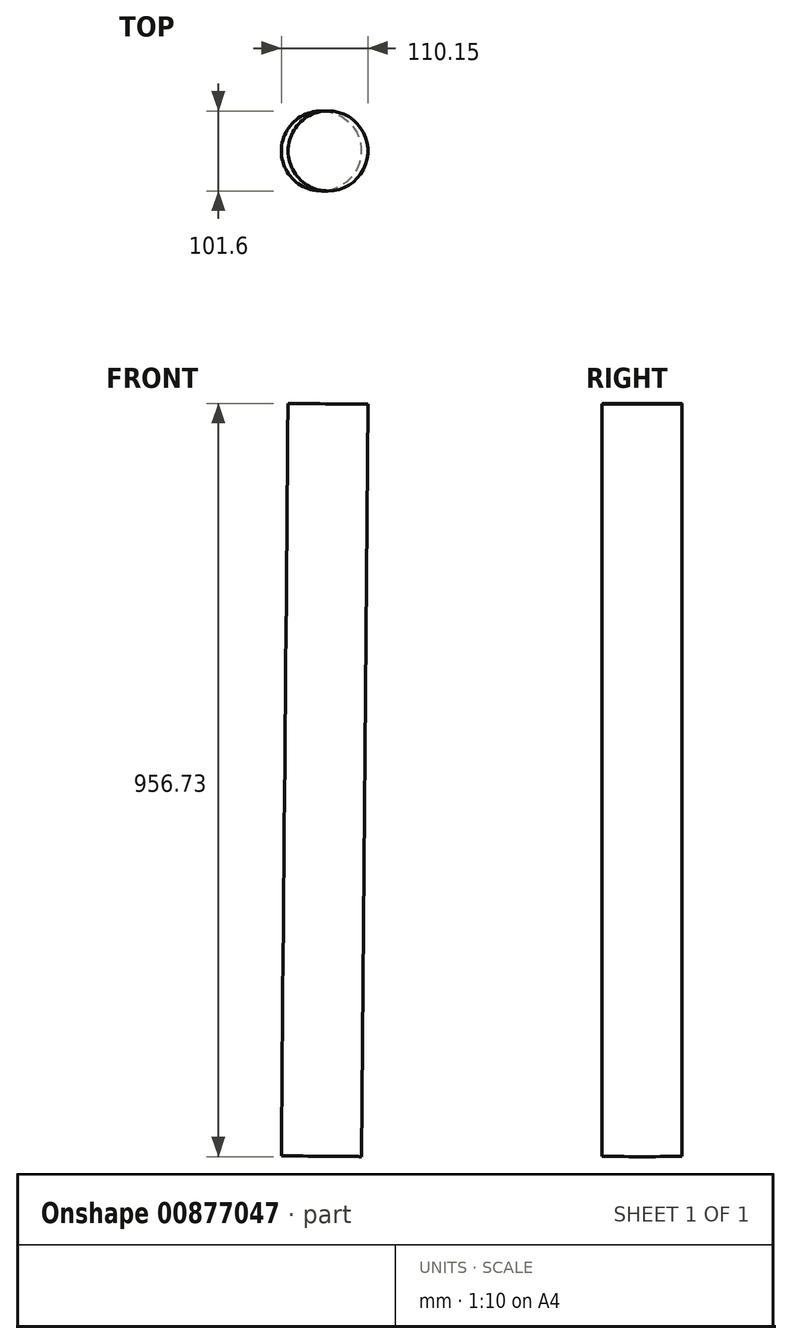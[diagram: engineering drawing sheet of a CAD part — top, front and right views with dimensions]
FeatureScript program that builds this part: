
annotation { "Feature Type Name" : "Feature", "Feature Type Description" : "" }
export const myFeature = defineFeature(function(context is Context, id is Id, definition is map)
    precondition{}
    {
        {
            var Q0;
            Q0=qCreatedBy(makeId("Front.planeOp"),FACE);
            var sketch = newSketch(context, id + "F0", { "sketchPlane" : qUnion([Q0])});
            skCircle(sketch, "E0", {"center": v(-120.6, -501.7) * mm, "radius": 120.6 * mm});
            skLineSegment(sketch, "E1", {"start": v(0, 0) * mm, "end": v(-169.13, -22.38) * mm});
            skLineSegment(sketch, "E2", {"start": v(-169.13, -22.38) * mm, "end": v(-239.94, -519.06) * mm});
            skLineSegment(sketch, "E3", {"start": v(0, 0) * mm, "end": v(161.78, 142.97) * mm});
            skLineSegment(sketch, "E4", {"start": v(161.15, 73.12) * mm, "end": v(152.6, -882.7) * mm});
            skLineSegment(sketch, "E5", {"start": v(161.15, 73.12) * mm, "end": v(161.78, 142.97) * mm});
            skCircle(sketch, "E6", {"center": v(0, 0) * mm, "radius": 31.75 * mm});
            skSolve(sketch);
        }
        {
            var Q0;
            Q0=sQuery(id+"F0.wireOp",EDGE,"E4");
            var Q1;
            Q1=qBodyType(qCreatedBy(id+"F2",EDGE),BodyType.WIRE);
            cPlane(context, id + "F1", {"entities" : qUnion([Q0, Q1]), "cplaneType" : CPlaneType.MID_PLANE, "offset" : 25 * mm, "width" : 150 * mm, "height" : 150 * mm});
        }
        {
            var Q0;
            Q0=qCreatedBy(id+"F1.planeOp",FACE);
            var sketch = newSketch(context, id + "F2", { "sketchPlane" : qUnion([Q0])});
            skCircle(sketch, "E7", {"center": v(160.5, 0) * mm, "radius": 50.8 * mm});
            skSolve(sketch);
        }
        {
            var Q0;
            Q0=makeQuery(id+"F2.imprint","IMPRINT",FACE,{"disambiguationData":[TD([[makeQuery(id+"F2.imprint","IMPRINT",EDGE,{"derivedFrom":sQuery(id+"F2.wireOp",EDGE,"E7")}),1.0]])]});
            var Q1;
            Q1=sQuery(id+"F0.wireOp",EDGE,"E4");
            sweep(context, id + "F3", {"profiles" : qUnion([Q0]), "path" : qUnion([Q1])});
        }
    });
